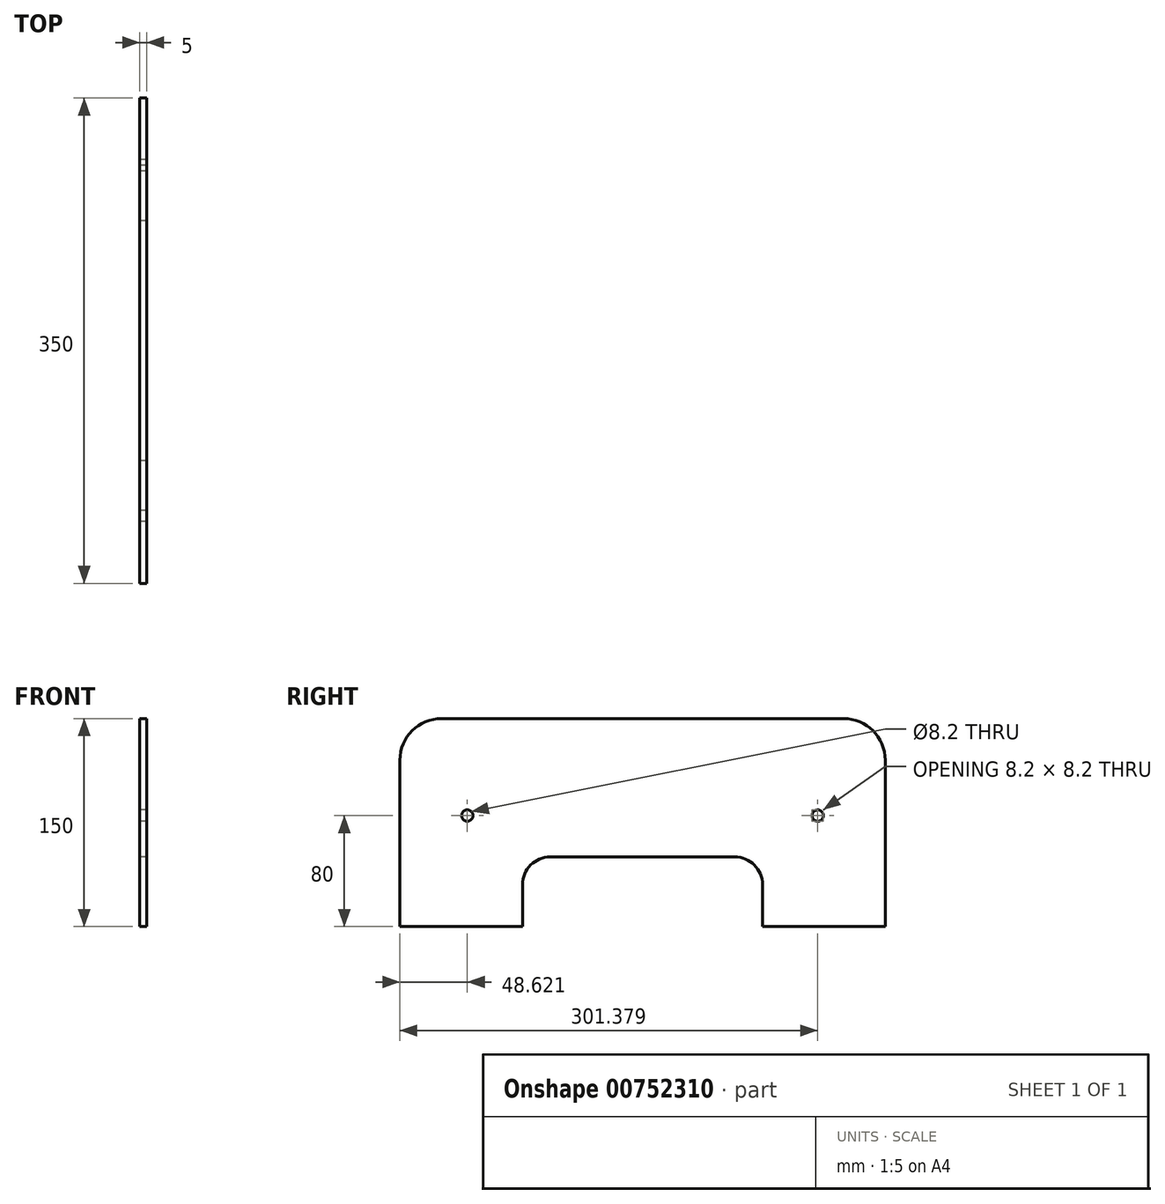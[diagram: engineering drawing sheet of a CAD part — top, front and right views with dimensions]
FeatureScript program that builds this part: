
annotation { "Feature Type Name" : "Feature", "Feature Type Description" : "" }
export const myFeature = defineFeature(function(context is Context, id is Id, definition is map)
    precondition{}
    {
        {
            var Q0;
            Q0=qCreatedBy(makeId("Right.planeOp"),FACE);
            var sketch = newSketch(context, id + "F0", { "sketchPlane" : qUnion([Q0])});
            skLineSegment(sketch, "E0.bottom", {"start": v(175, -75) * mm, "end": v(86.54, -75) * mm});
            skLineSegment(sketch, "E0.top", {"start": v(145, 75) * mm, "end": v(4, 75) * mm});
            skLineSegment(sketch, "E0.left", {"start": v(175, -75) * mm, "end": v(175, 45) * mm});
            skLineSegment(sketch, "E0.right", {"start": v(-175, -75) * mm, "end": v(-175, 45) * mm});
            skPoint(sketch, "E0.middle", {"position": v(0, 0) * mm});
            skLineSegment(sketch, "E1", {"start": v(0, 105) * mm, "end": v(0, -70) * mm, "construction": true});
            skLineSegment(sketch, "E2.trimOffspring", {"start": v(-4, 75) * mm, "end": v(-145, 75) * mm});
            skPoint(sketch, "E3.orphan", {"position": v(-166.8, 75) * mm});
            skCircle(sketch, "E4", {"center": v(-126.38, 5) * mm, "radius": 4.1 * mm});
            skLineSegment(sketch, "E5.left", {"start": v(-126.26, 9.1) * mm, "end": v(-126.26, 0.9) * mm});
            skPoint(sketch, "E6.left.end.orphan", {"position": v(4, 105) * mm});
            skPoint(sketch, "E6.right.end.orphan", {"position": v(-4, 105) * mm});
            skLineSegment(sketch, "E7", {"start": v(-4, 75) * mm, "end": v(4, 75) * mm});
            skCircle(sketch, "E8", {"center": v(0, 105) * mm, "radius": 150 * mm, "construction": true});
            skPoint(sketch, "E5.right.end.orphan", {"position": v(140.09, -4.1) * mm});
            skPoint(sketch, "E9.center.orphan", {"position": v(140.09, 0) * mm});
            skCircle(sketch, "E10", {"center": v(-126.38, 5) * mm, "radius": 11 * mm, "construction": true});
            skCircle(sketch, "E11", {"center": v(126.38, 5) * mm, "radius": 4.1 * mm});
            skLineSegment(sketch, "E12.left", {"start": v(126.5, 9.1) * mm, "end": v(126.5, 0.9) * mm});
            skCircle(sketch, "E13", {"center": v(126.38, 5) * mm, "radius": 11 * mm, "construction": true});
            skLineSegment(sketch, "E14.bottom", {"start": v(126.5, 9.1) * mm, "end": v(126.26, 9.1) * mm});
            skLineSegment(sketch, "E14.top", {"start": v(126.5, 0.9) * mm, "end": v(126.38, 0.9) * mm});
            skPoint(sketch, "E15.visualSharp", {"position": v(-175, 75) * mm});
            skArc(sketch, "E15.filletArc", {"start": v(-145, 75) * mm, "mid": v(-166.21, 66.21) * mm, "end": v(-175, 45) * mm});
            skPoint(sketch, "E16.visualSharp", {"position": v(175, 75) * mm});
            skArc(sketch, "E16.filletArc", {"start": v(175, 45) * mm, "mid": v(166.21, 66.21) * mm, "end": v(145, 75) * mm});
            skLineSegment(sketch, "E17.top", {"start": v(0, -24.79) * mm, "end": v(-66.54, -24.79) * mm});
            skLineSegment(sketch, "E17.left", {"start": v(0, -70) * mm, "end": v(0, -24.79) * mm});
            skLineSegment(sketch, "E17.right", {"start": v(-86.54, -75) * mm, "end": v(-86.54, -44.79) * mm});
            skPoint(sketch, "E18.visualSharp", {"position": v(-86.54, -24.79) * mm});
            skArc(sketch, "E18.filletArc", {"start": v(-66.54, -24.79) * mm, "mid": v(-80.68, -30.65) * mm, "end": v(-86.54, -44.79) * mm});
            skLineSegment(sketch, "E19.MirrorCS", {"start": v(0, -24.79) * mm, "end": v(66.54, -24.79) * mm});
            skArc(sketch, "E20.MirrorCS", {"start": v(66.54, -24.79) * mm, "mid": v(80.68, -30.65) * mm, "end": v(86.54, -44.79) * mm});
            skLineSegment(sketch, "E21.MirrorCS", {"start": v(86.54, -75) * mm, "end": v(86.54, -44.79) * mm});
            skLineSegment(sketch, "E22.trimOffspring", {"start": v(-86.54, -75) * mm, "end": v(-175, -75) * mm});
            skPoint(sketch, "E23.orphan", {"position": v(0, -75) * mm});
            skSolve(sketch);
        }
        {
            var Q0;
            Q0=qSketchRegion(id+"F0",true);
            extrude(context, id + "F1", {"entities" : qUnion([Q0]), "depth" : 5 * mm});
        }
    });
